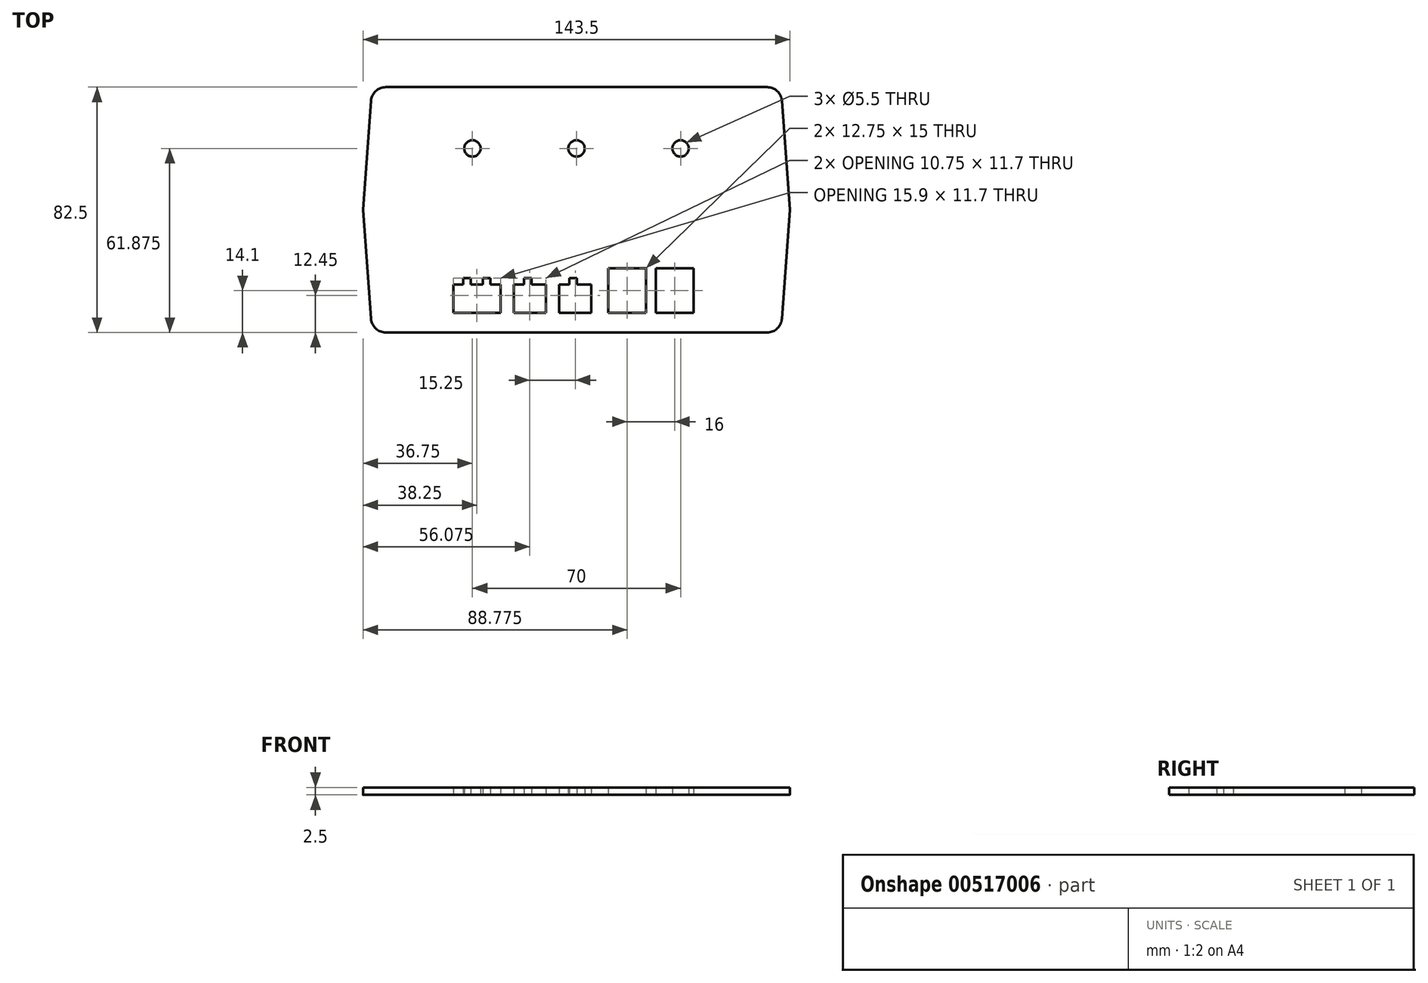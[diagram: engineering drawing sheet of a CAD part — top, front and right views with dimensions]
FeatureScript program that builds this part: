
annotation { "Feature Type Name" : "Feature", "Feature Type Description" : "" }
export const myFeature = defineFeature(function(context is Context, id is Id, definition is map)
    precondition{}
    {
        {
            var Q0;
            Q0=qCreatedBy(makeId("Top.planeOp"),FACE);
            var sketch = newSketch(context, id + "F0", { "sketchPlane" : qUnion([Q0])});
            skLineSegment(sketch, "E0", {"start": v(-71.75, 0) * mm, "end": v(71.75, 0) * mm, "construction": true});
            skLineSegment(sketch, "E1", {"start": v(0, 41.25) * mm, "end": v(0, -41.25) * mm, "construction": true});
            skLineSegment(sketch, "E2.bottom", {"start": v(64.1, 41.25) * mm, "end": v(-64.1, 41.25) * mm});
            skLineSegment(sketch, "E2.top", {"start": v(64.1, -41.25) * mm, "end": v(-64.1, -41.25) * mm});
            skLineSegment(sketch, "E2.left", {"start": v(71.75, 41.25) * mm, "end": v(71.75, -41.25) * mm, "construction": true});
            skLineSegment(sketch, "E2.right", {"start": v(-71.75, 41.25) * mm, "end": v(-71.75, -41.25) * mm, "construction": true});
            skPoint(sketch, "E2.middle", {"position": v(0, 0) * mm});
            skLineSegment(sketch, "E3", {"start": v(71.75, 0) * mm, "end": v(69.09, 36.61) * mm});
            skLineSegment(sketch, "E4", {"start": v(71.75, 0) * mm, "end": v(69.09, -36.61) * mm});
            skLineSegment(sketch, "E5", {"start": v(-71.75, 0) * mm, "end": v(-69.09, 36.61) * mm});
            skLineSegment(sketch, "E6", {"start": v(-71.75, 0) * mm, "end": v(-69.09, -36.61) * mm});
            skLineSegment(sketch, "E7", {"start": v(69.23, -34.65) * mm, "end": v(-69.23, -34.65) * mm, "construction": true});
            skLineSegment(sketch, "E8.bottom", {"start": v(39.4, -34.65) * mm, "end": v(26.65, -34.65) * mm});
            skLineSegment(sketch, "E8.top", {"start": v(39.4, -19.65) * mm, "end": v(26.65, -19.65) * mm});
            skLineSegment(sketch, "E8.left", {"start": v(39.4, -34.65) * mm, "end": v(39.4, -19.65) * mm});
            skLineSegment(sketch, "E8.right", {"start": v(26.65, -34.65) * mm, "end": v(26.65, -19.65) * mm});
            skLineSegment(sketch, "E9.bottom", {"start": v(23.4, -34.65) * mm, "end": v(10.65, -34.65) * mm});
            skLineSegment(sketch, "E9.top", {"start": v(23.4, -19.65) * mm, "end": v(10.65, -19.65) * mm});
            skLineSegment(sketch, "E9.left", {"start": v(23.4, -34.65) * mm, "end": v(23.4, -19.65) * mm});
            skLineSegment(sketch, "E9.right", {"start": v(10.65, -34.65) * mm, "end": v(10.65, -19.65) * mm});
            skLineSegment(sketch, "E10.bottom", {"start": v(4.95, -34.65) * mm, "end": v(-5.8, -34.65) * mm});
            skLineSegment(sketch, "E10.top", {"start": v(4.95, -25.15) * mm, "end": v(0.1, -25.15) * mm});
            skLineSegment(sketch, "E10.left", {"start": v(4.95, -34.65) * mm, "end": v(4.95, -25.15) * mm});
            skLineSegment(sketch, "E10.right", {"start": v(-5.8, -34.65) * mm, "end": v(-5.8, -25.15) * mm});
            skLineSegment(sketch, "E11.top", {"start": v(0.1, -22.95) * mm, "end": v(-2.4, -22.95) * mm});
            skLineSegment(sketch, "E11.left", {"start": v(0.1, -25.15) * mm, "end": v(0.1, -22.95) * mm});
            skLineSegment(sketch, "E11.right", {"start": v(-2.4, -25.15) * mm, "end": v(-2.4, -22.95) * mm});
            skLineSegment(sketch, "E12.trimOffspring", {"start": v(-2.4, -25.15) * mm, "end": v(-5.8, -25.15) * mm});
            skLineSegment(sketch, "E13.bottom", {"start": v(-10.3, -34.65) * mm, "end": v(-21.05, -34.65) * mm});
            skLineSegment(sketch, "E13.top", {"start": v(-10.3, -25.15) * mm, "end": v(-15.15, -25.15) * mm});
            skLineSegment(sketch, "E13.left", {"start": v(-10.3, -34.65) * mm, "end": v(-10.3, -25.15) * mm});
            skLineSegment(sketch, "E13.right", {"start": v(-21.05, -34.65) * mm, "end": v(-21.05, -25.15) * mm});
            skLineSegment(sketch, "E14.bottom", {"start": v(-25.55, -34.65) * mm, "end": v(-41.45, -34.65) * mm});
            skLineSegment(sketch, "E14.top", {"start": v(-25.55, -25.15) * mm, "end": v(-28.95, -25.15) * mm});
            skLineSegment(sketch, "E14.left", {"start": v(-25.55, -34.65) * mm, "end": v(-25.55, -25.15) * mm});
            skLineSegment(sketch, "E14.right", {"start": v(-41.45, -34.65) * mm, "end": v(-41.45, -25.15) * mm});
            skLineSegment(sketch, "E15.top", {"start": v(-15.15, -22.95) * mm, "end": v(-17.65, -22.95) * mm});
            skLineSegment(sketch, "E15.left", {"start": v(-15.15, -25.15) * mm, "end": v(-15.15, -22.95) * mm});
            skLineSegment(sketch, "E15.right", {"start": v(-17.65, -25.15) * mm, "end": v(-17.65, -22.95) * mm});
            skLineSegment(sketch, "E16.top", {"start": v(-35.55, -22.95) * mm, "end": v(-38.05, -22.95) * mm});
            skLineSegment(sketch, "E16.left", {"start": v(-35.55, -25.15) * mm, "end": v(-35.55, -22.95) * mm});
            skLineSegment(sketch, "E16.right", {"start": v(-38.05, -25.15) * mm, "end": v(-38.05, -22.95) * mm});
            skLineSegment(sketch, "E17.trimOffspring", {"start": v(-17.65, -25.15) * mm, "end": v(-21.05, -25.15) * mm});
            skLineSegment(sketch, "E18.trimOffspring", {"start": v(-38.05, -25.15) * mm, "end": v(-41.45, -25.15) * mm});
            skLineSegment(sketch, "E19.top", {"start": v(-28.95, -22.95) * mm, "end": v(-31.45, -22.95) * mm});
            skLineSegment(sketch, "E19.left", {"start": v(-28.95, -25.15) * mm, "end": v(-28.95, -22.95) * mm});
            skLineSegment(sketch, "E19.right", {"start": v(-31.45, -25.15) * mm, "end": v(-31.45, -22.95) * mm});
            skLineSegment(sketch, "E20.trimOffspring", {"start": v(-31.45, -25.15) * mm, "end": v(-35.55, -25.15) * mm});
            skLineSegment(sketch, "E21.bottom", {"start": v(-50.9, -34.65) * mm, "end": v(50.9, -34.65) * mm, "construction": true});
            skLineSegment(sketch, "E21.top", {"start": v(-50.9, -35.65) * mm, "end": v(50.9, -35.65) * mm, "construction": true});
            skLineSegment(sketch, "E21.left", {"start": v(-50.9, -34.65) * mm, "end": v(-50.9, -35.65) * mm, "construction": true});
            skLineSegment(sketch, "E21.right", {"start": v(50.9, -34.65) * mm, "end": v(50.9, -35.65) * mm, "construction": true});
            skPoint(sketch, "E22", {"position": v(0, -35.65) * mm});
            skLineSegment(sketch, "E23", {"start": v(70.25, 20.62) * mm, "end": v(-70.25, 20.62) * mm, "construction": true});
            skCircle(sketch, "E24", {"center": v(0, 20.62) * mm, "radius": 2.75 * mm});
            skCircle(sketch, "E25", {"center": v(35, 20.63) * mm, "radius": 2.75 * mm});
            skCircle(sketch, "E26", {"center": v(-35, 20.62) * mm, "radius": 2.75 * mm});
            skLineSegment(sketch, "E27", {"start": v(4.95, -25.15) * mm, "end": v(-41.45, -25.15) * mm, "construction": true});
            skLineSegment(sketch, "E28", {"start": v(0.1, -22.95) * mm, "end": v(-38.05, -22.95) * mm, "construction": true});
            skLineSegment(sketch, "E29", {"start": v(10.65, -19.65) * mm, "end": v(39.4, -19.65) * mm, "construction": true});
            skPoint(sketch, "E30.visualSharp", {"position": v(-68.75, 41.25) * mm});
            skArc(sketch, "E30.filletArc", {"start": v(-64.1, 41.25) * mm, "mid": v(-67.5, 39.91) * mm, "end": v(-69.09, 36.61) * mm});
            skPoint(sketch, "E31.visualSharp", {"position": v(68.75, 41.25) * mm});
            skArc(sketch, "E31.filletArc", {"start": v(69.09, 36.61) * mm, "mid": v(67.5, 39.91) * mm, "end": v(64.1, 41.25) * mm});
            skPoint(sketch, "E32.visualSharp", {"position": v(68.75, -41.25) * mm});
            skArc(sketch, "E32.filletArc", {"start": v(64.1, -41.25) * mm, "mid": v(67.5, -39.91) * mm, "end": v(69.09, -36.61) * mm});
            skPoint(sketch, "E33.visualSharp", {"position": v(-68.75, -41.25) * mm});
            skArc(sketch, "E33.filletArc", {"start": v(-69.09, -36.61) * mm, "mid": v(-67.5, -39.91) * mm, "end": v(-64.1, -41.25) * mm});
            skSolve(sketch);
        }
        {
            var Q0;
            Q0=qSketchRegion(id+"F0",true);
            extrude(context, id + "F1", {"entities" : qUnion([Q0]), "depth" : 2.5 * mm, "offsetDistance" : 25 * mm});
        }
        {
            var Q0;
            Q0=makeQuery(id+"F1.opExtrude","SWEPT_EDGE",EDGE,{"disambiguationData":[OSD([sQuery(id+"F0.wireOp",EDGE,"E2.top"),sQuery(id+"F0.wireOp",EDGE,"E6")])]});
            var Q1;
            Q1=makeQuery(id+"F1.opExtrude","SWEPT_EDGE",EDGE,{"disambiguationData":[OSD([sQuery(id+"F0.wireOp",EDGE,"E2.bottom"),sQuery(id+"F0.wireOp",EDGE,"E5")])]});
            var Q2;
            Q2=makeQuery(id+"F1.opExtrude","SWEPT_EDGE",EDGE,{"disambiguationData":[OSD([sQuery(id+"F0.wireOp",EDGE,"E2.bottom"),sQuery(id+"F0.wireOp",EDGE,"E3")])]});
            var Q3;
            Q3=makeQuery(id+"F1.opExtrude","SWEPT_EDGE",EDGE,{"disambiguationData":[OSD([sQuery(id+"F0.wireOp",EDGE,"E2.top"),sQuery(id+"F0.wireOp",EDGE,"E4")])]});
            fillet(context, id + "F2", {"entities" : qUnion([Q0, Q1, Q2, Q3]), "radius" : 1.5 * mm, "tangentPropagation" : true, "allowEdgeOverflow" : false});
        }
    });
